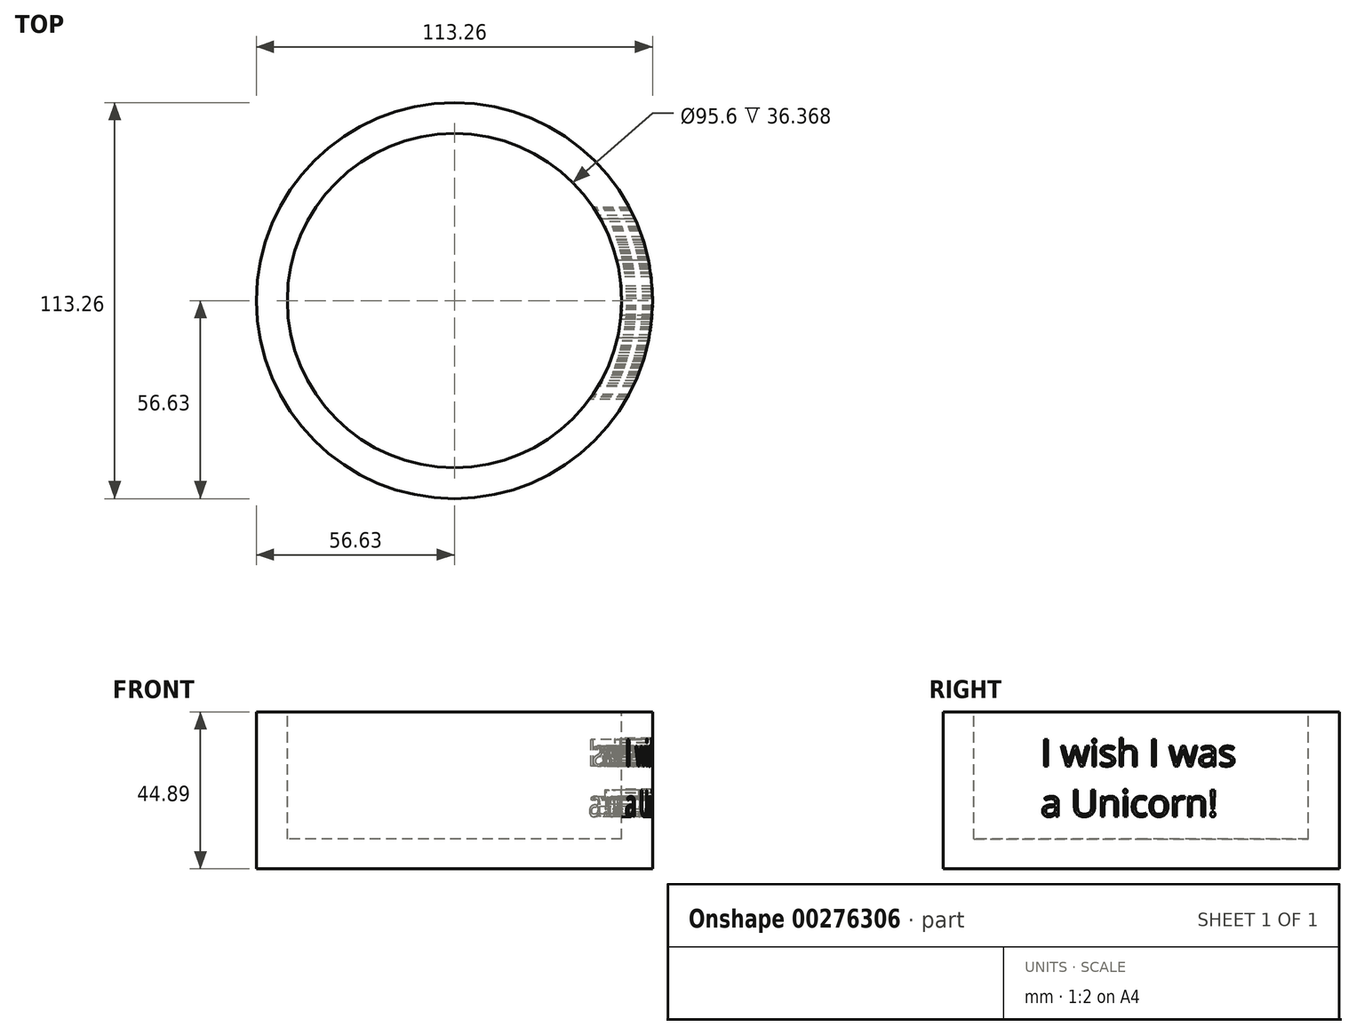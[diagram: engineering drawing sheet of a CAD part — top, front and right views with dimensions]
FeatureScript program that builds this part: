
annotation { "Feature Type Name" : "Feature", "Feature Type Description" : "" }
export const myFeature = defineFeature(function(context is Context, id is Id, definition is map)
    precondition{}
    {
        {
            var Q0;
            Q0=qCreatedBy(makeId("Front.planeOp"),FACE);
            var sketch = newSketch(context, id + "F0", { "sketchPlane" : qUnion([Q0])});
            skLineSegment(sketch, "E0", {"start": v(0, 44.89) * mm, "end": v(8.83, 44.89) * mm});
            skLineSegment(sketch, "E1", {"start": v(8.83, 44.89) * mm, "end": v(8.83, 8.52) * mm});
            skLineSegment(sketch, "E2", {"start": v(8.83, 8.52) * mm, "end": v(56.63, 8.52) * mm});
            skLineSegment(sketch, "E3", {"start": v(56.63, 8.52) * mm, "end": v(56.63, 0) * mm});
            skLineSegment(sketch, "E4", {"start": v(56.63, 0) * mm, "end": v(0, 0) * mm});
            skLineSegment(sketch, "E5", {"start": v(0, 0) * mm, "end": v(0, 44.89) * mm});
            skSolve(sketch);
        }
        {
            var Q0;
            Q0=makeQuery(id+"F0.imprint","IMPRINT",FACE,{"disambiguationData":[TD([[makeQuery(id+"F0.imprint","IMPRINT",EDGE,{"derivedFrom":sQuery(id+"F0.wireOp",EDGE,"E0")}),-1.0]])]});
            var Q1;
            Q1=sQuery(id+"F0.wireOp",EDGE,"E3");
            revolve(context, id + "F1", {"entities" : qUnion([Q0]), "axis" : qUnion([Q1]), "revolveType" : RevolveType.FULL});
        }
        {
            var Q0;
            Q0=qCreatedBy(makeId("Right.planeOp"),FACE);
            cPlane(context, id + "F2", {"entities" : qUnion([Q0]), "cplaneType" : CPlaneType.OFFSET, "offset" : 57.15 * mm, "width" : 152.4 * mm, "height" : 152.4 * mm});
        }
        {
            var Q0;
            Q0=qCreatedBy(id+"F2.planeOp",FACE);
            var sketch = newSketch(context, id + "F3", { "sketchPlane" : qUnion([Q0])});
            skText(sketch, "E6", { "text": "I wish I was\na Unicorn!", "fontName": "OpenSans-Regular.ttf"});
            const initialGuessF3  = {"E6": [-0.0287, 0.0294, 1, 0, 0.00762]};
            skSetInitialGuess(sketch, initialGuessF3);
            skSolve(sketch);
        }
        {
            var Q0;
            Q0 = qSketchRegion(id + "F3", true);
            extrude(context, id + "F4", {"entities" : qUnion([Q0]), "operationType" : NewBodyOperationType.REMOVE, "depth" : 114.3 * mm});
        }
    });
